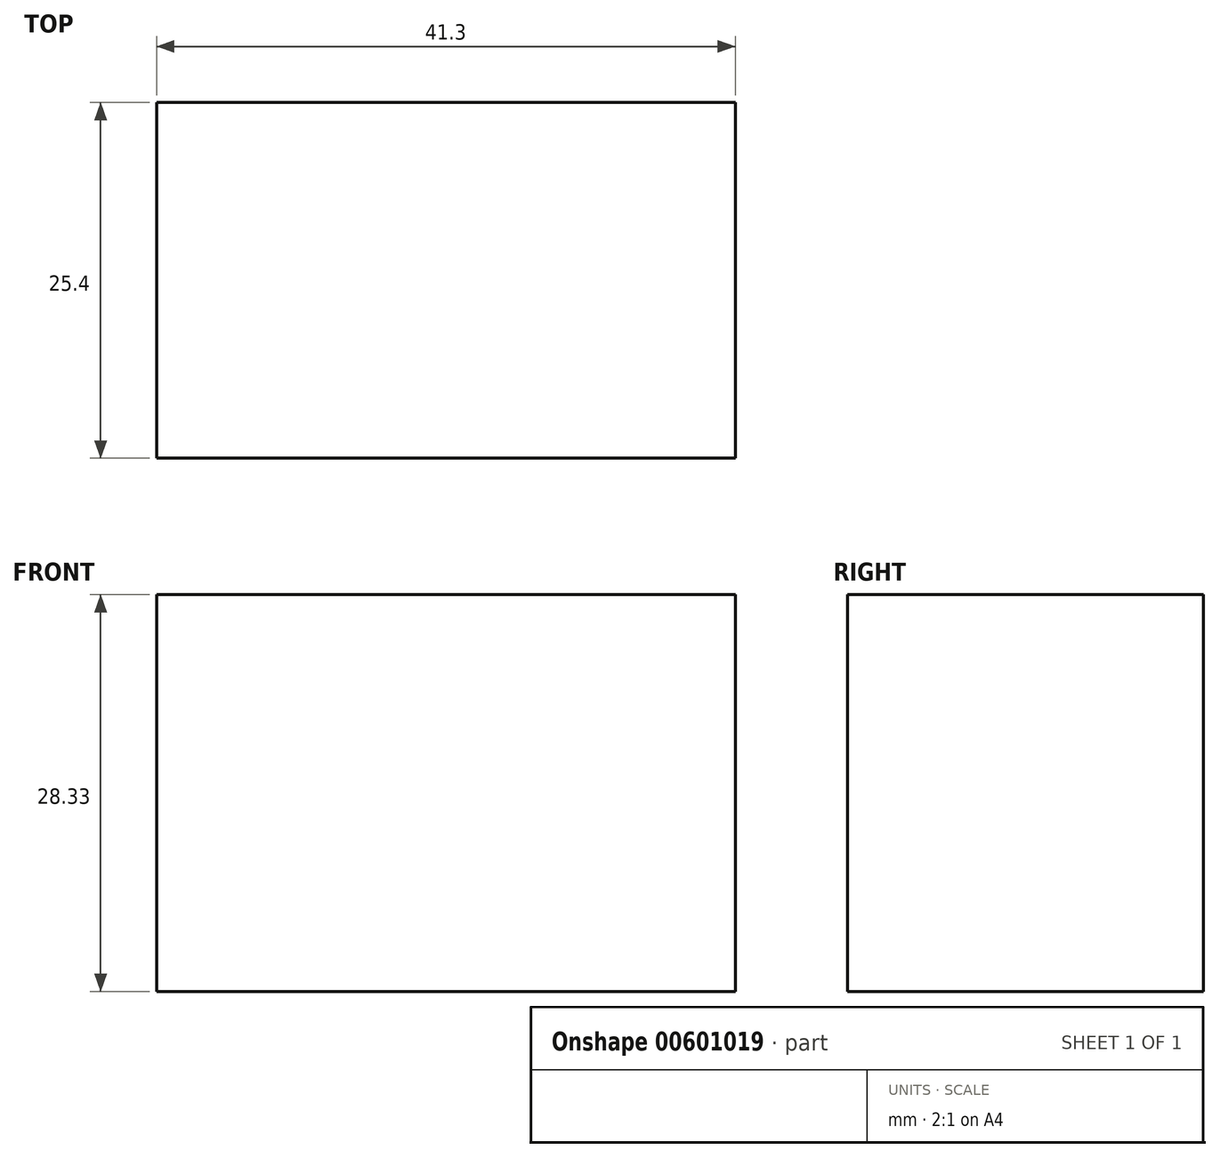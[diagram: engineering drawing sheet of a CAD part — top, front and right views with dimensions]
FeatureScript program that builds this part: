
annotation { "Feature Type Name" : "Feature", "Feature Type Description" : "" }
export const myFeature = defineFeature(function(context is Context, id is Id, definition is map)
    precondition{}
    {
        {
            var Q0;
            Q0=qCreatedBy(makeId("Front.planeOp"),FACE);
            var sketch = newSketch(context, id + "F0", { "sketchPlane" : qUnion([Q0])});
            skLineSegment(sketch, "E0.bottom", {"start": v(-21.2, 12.02) * mm, "end": v(20.1, 12.02) * mm});
            skLineSegment(sketch, "E0.top", {"start": v(-21.2, -16.31) * mm, "end": v(20.1, -16.31) * mm});
            skLineSegment(sketch, "E0.left", {"start": v(-21.2, 12.02) * mm, "end": v(-21.2, -16.31) * mm});
            skLineSegment(sketch, "E0.right", {"start": v(20.1, 12.02) * mm, "end": v(20.1, -16.31) * mm});
            skSolve(sketch);
        }
        {
            var Q0;
            Q0=makeQuery(id+"F0.imprint","IMPRINT",FACE,{"disambiguationData":[TD([[makeQuery(id+"F0.imprint","IMPRINT",EDGE,{"derivedFrom":sQuery(id+"F0.wireOp",EDGE,"E0.bottom")}),-1.0]])]});
            extrude(context, id + "F1", {"entities" : qUnion([Q0]), "depth" : 25.4 * mm, "offsetDistance" : 25.4 * mm});
        }
    });
